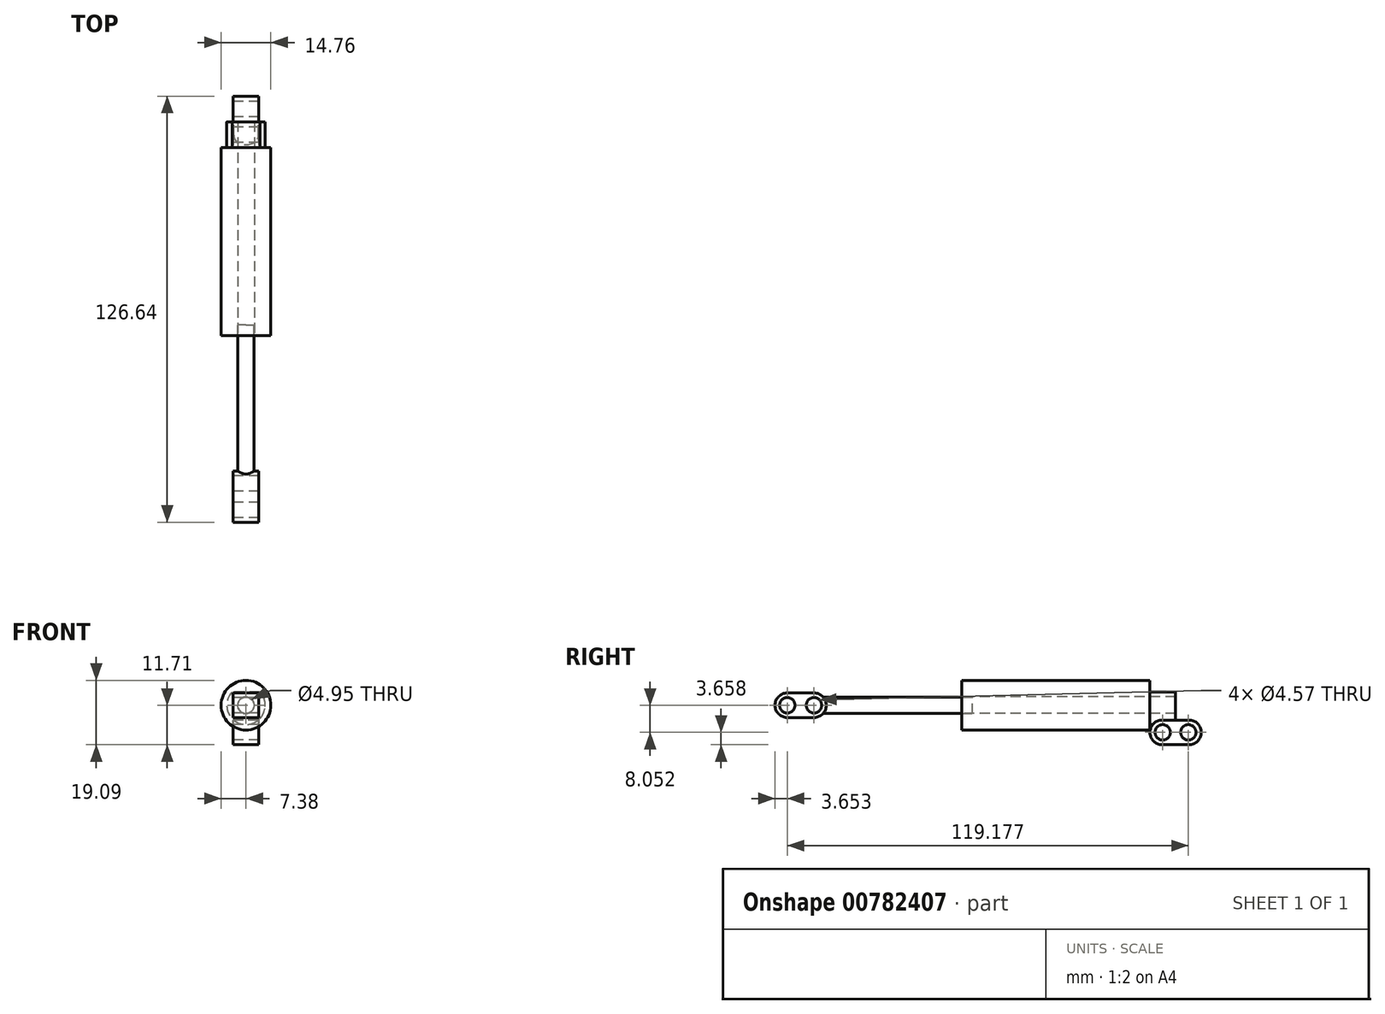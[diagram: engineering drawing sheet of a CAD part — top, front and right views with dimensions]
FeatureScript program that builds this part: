
annotation { "Feature Type Name" : "Feature", "Feature Type Description" : "" }
export const myFeature = defineFeature(function(context is Context, id is Id, definition is map)
    precondition{}
    {
        {
            var Q0;
            Q0=qCreatedBy(makeId("Front.planeOp"),FACE);
            cPlane(context, id + "F0", {"entities" : qUnion([Q0]), "cplaneType" : CPlaneType.OFFSET, "offset" : 28.57 * mm, "width" : 152.4 * mm, "height" : 152.4 * mm});
        }
        {
            var Q0;
            Q0=qCreatedBy(makeId("Front.planeOp"),FACE);
            var sketch = newSketch(context, id + "F1", { "sketchPlane" : qUnion([Q0])});
            skCircle(sketch, "E0", {"center": v(0, 0) * mm, "radius": 7.38 * mm});
            skSolve(sketch);
        }
        {
            var Q0;
            Q0=qSketchRegion(id+"F1",true);
            extrude(context, id + "F2", {"entities" : qUnion([Q0]), "endBound" : BoundingType.SYMMETRIC, "depth" : 63.5 * mm, "offsetDistance" : 25.4 * mm});
        }
        {
            var Q0;
            Q0=makeQuery(id+"F2.opExtrude","CAP_FACE",FACE,{"disambiguationData":[OSD([sQuery(id+"F1.wireOp",EDGE,"E0")])],"isStart":false});
            var sketch = newSketch(context, id + "F3", { "sketchPlane" : qUnion([Q0])});
            skCircle(sketch, "E1", {"center": v(0, 0) * mm, "radius": 2.48 * mm});
            skSolve(sketch);
        }
        {
            var Q0;
            Q0=qSketchRegion(id+"F3",true);
            var Q1;
            Q1=makeQuery(id+"F2.opExtrude","CAP_FACE",FACE,{"disambiguationData":[OSD([sQuery(id+"F1.wireOp",EDGE,"E0")])],"isStart":true});
            extrude(context, id + "F4", {"entities" : qUnion([Q0]), "operationType" : NewBodyOperationType.REMOVE, "endBound" : BoundingType.UP_TO_SURFACE, "oppositeDirection" : true, "depth" : 50.8 * mm, "endBoundEntityFace" : qUnion([Q1]), "offsetDistance" : 25.4 * mm});
        }
        {
            var Q0;
            Q0=makeQuery(id+"F2.opExtrude","CAP_FACE",FACE,{"disambiguationData":[OSD([sQuery(id+"F1.wireOp",EDGE,"E0")])],"isStart":true});
            var sketch = newSketch(context, id + "F5", { "sketchPlane" : qUnion([Q0])});
            skCircle(sketch, "E2", {"center": v(0, 0) * mm, "radius": 3.18 * mm, "construction": true});
            skArc(sketch, "E3.0", {"start": v(-4.14, 3.94) * mm, "mid": v(0, -5.72) * mm, "end": v(4.14, 3.94) * mm});
            skLineSegment(sketch, "E4", {"start": v(-4.14, 3.94) * mm, "end": v(4.14, 3.94) * mm});
            skCircle(sketch, "E5.0", {"center": v(0, 0) * mm, "radius": 7.38 * mm});
            skSolve(sketch);
        }
        {
            var Q0;
            Q0=qSketchRegion(id+"F5",true);
            extrude(context, id + "F6", {"entities" : qUnion([Q0]), "operationType" : NewBodyOperationType.REMOVE, "oppositeDirection" : true, "depth" : 7.62 * mm, "offsetDistance" : 25.4 * mm});
        }
        {
            var Q0;
            Q0=qCreatedBy(makeId("Right.planeOp"),FACE);
            var sketch = newSketch(context, id + "F7", { "sketchPlane" : qUnion([Q0])});
            skArc(sketch, "E6", {"start": v(27.79, -4.4) * mm, "mid": v(24.13, -8.05) * mm, "end": v(27.79, -11.7) * mm});
            skLineSegment(sketch, "E7", {"start": v(24.13, -8.05) * mm, "end": v(39.37, -8.05) * mm, "construction": true});
            skArc(sketch, "E8", {"start": v(35.71, -11.7) * mm, "mid": v(39.37, -8.05) * mm, "end": v(35.71, -4.4) * mm});
            skLineSegment(sketch, "E9", {"start": v(27.79, -4.4) * mm, "end": v(35.71, -4.4) * mm});
            skLineSegment(sketch, "E10.MirrorCS", {"start": v(27.79, -11.7) * mm, "end": v(35.71, -11.7) * mm});
            skLineSegment(sketch, "E11.0", {"start": v(24.13, 3.94) * mm, "end": v(31.75, 3.94) * mm, "construction": true});
            skLineSegment(sketch, "E12.1", {"start": v(24.13, -7.38) * mm, "end": v(24.13, 7.38) * mm, "construction": true});
            skCircle(sketch, "E13", {"center": v(35.56, -8.05) * mm, "radius": 2.29 * mm});
            skLineSegment(sketch, "E14", {"start": v(31.75, -4.4) * mm, "end": v(31.75, -11.7) * mm, "construction": true});
            skCircle(sketch, "E15.MirrorC", {"center": v(27.94, -8.05) * mm, "radius": 2.29 * mm});
            skSolve(sketch);
        }
        {
            var Q0;
            Q0=qSketchRegion(id+"F7",true);
            extrude(context, id + "F8", {"entities" : qUnion([Q0]), "operationType" : NewBodyOperationType.ADD, "endBound" : BoundingType.SYMMETRIC, "depth" : 7.62 * mm, "offsetDistance" : 25.4 * mm});
        }
        {
            var Q0;
            Q0=qCreatedBy(makeId("Right.planeOp"),FACE);
            var sketch = newSketch(context, id + "F9", { "sketchPlane" : qUnion([Q0])});
            skArc(sketch, "E16", {"start": v(-75.7, -3.66) * mm, "mid": v(-72.03, 0) * mm, "end": v(-75.7, 3.66) * mm});
            skArc(sketch, "E17", {"start": v(-83.62, 3.66) * mm, "mid": v(-87.27, 0) * mm, "end": v(-83.62, -3.66) * mm});
            skLineSegment(sketch, "E18", {"start": v(-87.27, 0) * mm, "end": v(-72.03, 0) * mm, "construction": true});
            skLineSegment(sketch, "E19", {"start": v(-83.62, 3.66) * mm, "end": v(-75.7, 3.66) * mm});
            skLineSegment(sketch, "E20.MirrorCS", {"start": v(-83.62, -3.66) * mm, "end": v(-75.7, -3.66) * mm});
            skCircle(sketch, "E21", {"center": v(-75.7, 0) * mm, "radius": 2.29 * mm});
            skCircle(sketch, "E22", {"center": v(-83.62, 0) * mm, "radius": 2.29 * mm});
            skSolve(sketch);
        }
        {
            var Q0;
            Q0=qSketchRegion(id+"F9",true);
            extrude(context, id + "F10", {"entities" : qUnion([Q0]), "endBound" : BoundingType.SYMMETRIC, "depth" : 7.62 * mm, "offsetDistance" : 25.4 * mm});
        }
        {
            var Q0;
            Q0=qCreatedBy(id+"F0.planeOp",FACE);
            var sketch = newSketch(context, id + "F11", { "sketchPlane" : qUnion([Q0])});
            skCircle(sketch, "E23", {"center": v(0, 0) * mm, "radius": 2.44 * mm});
            skSolve(sketch);
        }
        {
            var Q0;
            Q0=qSketchRegion(id+"F11",true);
            var Q1;
            Q1=makeQuery(id+"F10.opExtrude","SWEPT_BODY",BODY,{"disambiguationData":[OSD([sQuery(id+"F9.wireOp",EDGE,"E16"),sQuery(id+"F9.wireOp",EDGE,"E17"),sQuery(id+"F9.wireOp",EDGE,"E19"),sQuery(id+"F9.wireOp",EDGE,"E20.MirrorCS"),sQuery(id+"F9.wireOp",EDGE,"E21"),sQuery(id+"F9.wireOp",EDGE,"E22")])]});
            extrude(context, id + "F12", {"entities" : qUnion([Q0]), "operationType" : NewBodyOperationType.ADD, "endBound" : BoundingType.UP_TO_BODY, "depth" : 25.4 * mm, "endBoundEntityBody" : qUnion([Q1]), "offsetDistance" : 25.4 * mm});
        }
    });
